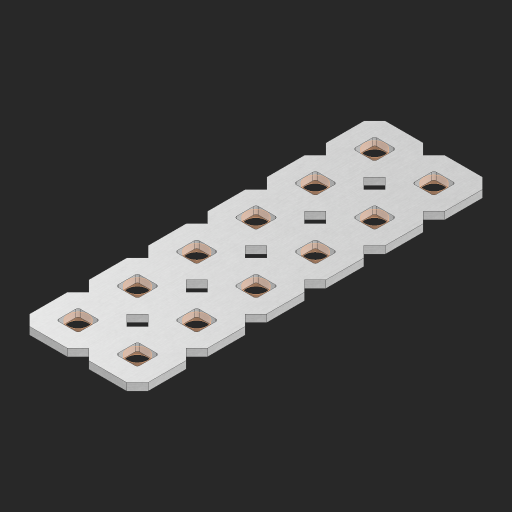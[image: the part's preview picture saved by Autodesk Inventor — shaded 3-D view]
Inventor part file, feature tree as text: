
AUTODESK INVENTOR PART (.ipt)
format: ipt  version: 2023 (Build 270158000, 158)  size: 423,424 bytes
history: native  units: in
note: dims shown in document units (in); Inventor stores cm internally (conversion verified against a paired STEP export)
features: other x13, extrude x11, sketch x2, pattern_linear x1
ambient origin geometry x8: Origin, YZ Plane, XZ Plane, XY Plane, X Axis, Y Axis, Z Axis, Center Point
bodies: Solid1 (feature_tree), Body (feature_tree)
feature tree (27):
  pattern_linear  "Rectangular Pattern1"  Spacing1=0.09in  [1 undecoded]
  sketch  "Sketch1"  dims[d1=0.5in]
  sketch  "Sketch2"  dims[d2=0.182in d3=0.09in d4=0.09in d5=0.09in d6=0.09in d7=0.09in d8=0.09in d9=0.09in d10=0.09in d11=0.02in d13=0.0in d14=0.172in d15=0.0625in d16=0.0in d19=0.5in d22=0.5in]
  other  "Srf1"
  other  "Srf126"
  other  "Srf127"
  other  "Srf128"
  other  "Srf129"
  other  "Srf130"
  other  "Srf268"
  other  "Srf269"
  other  "Srf270"
  other  "Srf271"
  other  "Srf272"
  other  "Srf273"
  other  "Circle"
  extrude  "ExtrusionSrf126"  Depth=0.09in
  extrude  "ExtrusionSrf127"  Depth=0.09in
  extrude  "ExtrusionSrf128"  Depth=0.09in
  extrude  "ExtrusionSrf129"  Depth=0.09in
  extrude  "ExtrusionSrf130"  Depth=0.09in
  extrude  "ExtrusionSrf268"  Depth=0.09in
  extrude  "ExtrusionSrf269"  Depth=0.09in
  extrude  "ExtrusionSrf270"  Depth=0.02in
  extrude  "ExtrusionSrf271"  TaperAngle=0.0deg  [1 undecoded]
  extrude  "ExtrusionSrf272"  Depth=0.5in
  extrude  "ExtrusionSrf273"  Depth=0.0625in TaperAngle=0.0deg
note: 2 required parameter values undecoded (feature->parameter linkage not recoverable at this tier; creation-order binding heuristic only, values carry confidence <= 0.55)
